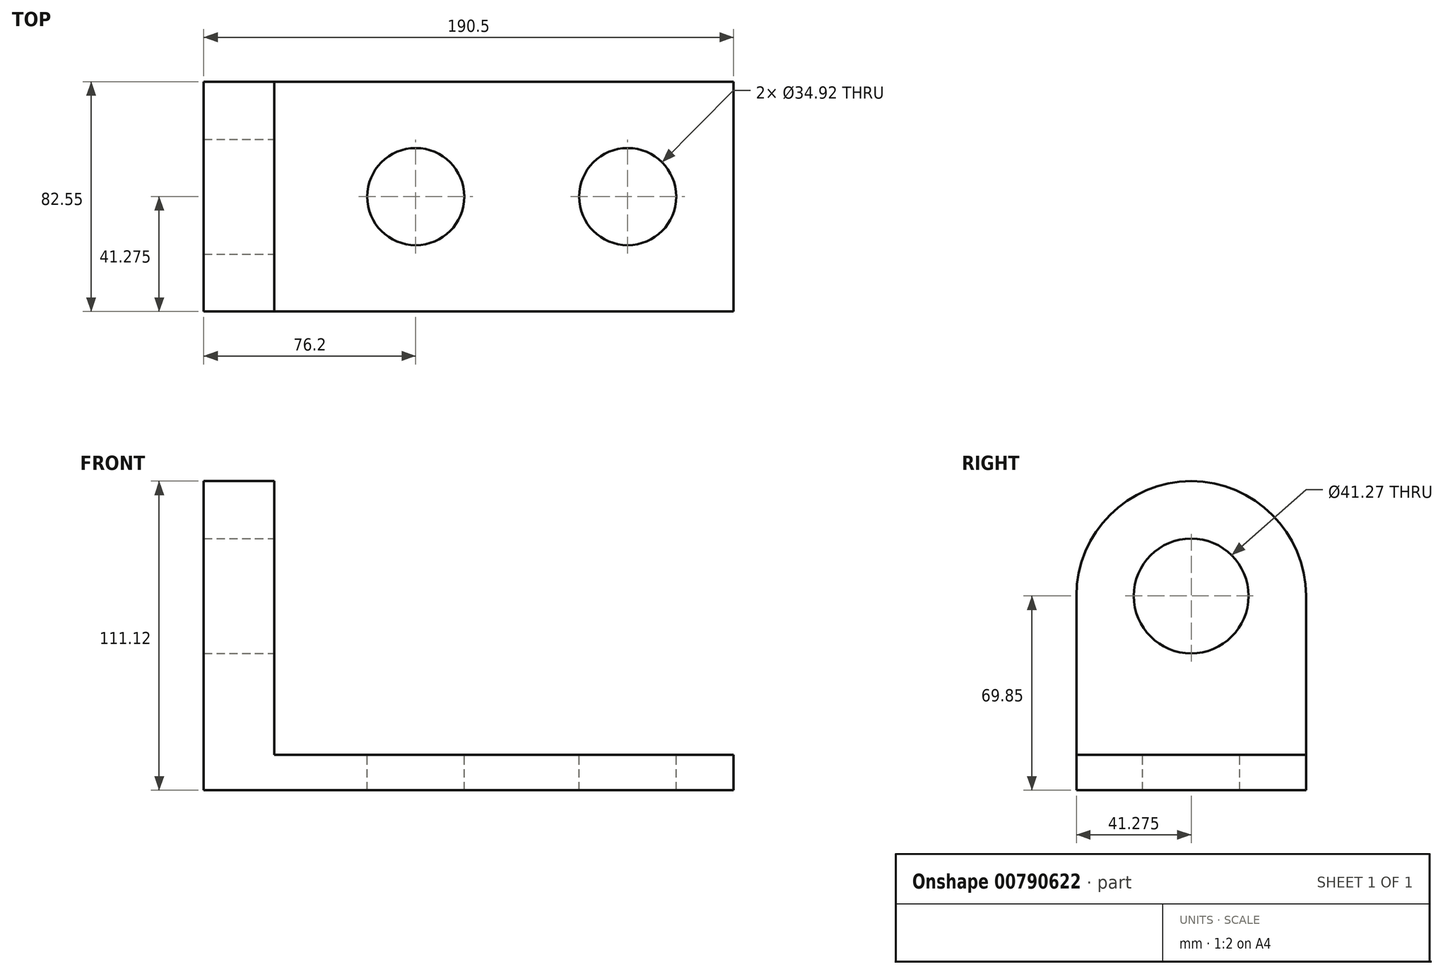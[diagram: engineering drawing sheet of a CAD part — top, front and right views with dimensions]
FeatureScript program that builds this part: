
annotation { "Feature Type Name" : "Feature", "Feature Type Description" : "" }
export const myFeature = defineFeature(function(context is Context, id is Id, definition is map)
    precondition{}
    {
        {
            var Q0;
            Q0=qCreatedBy(makeId("Front.planeOp"),FACE);
            var sketch = newSketch(context, id + "F0", { "sketchPlane" : qUnion([Q0])});
            skLineSegment(sketch, "E0", {"start": v(0, 0) * mm, "end": v(-95.25, 0) * mm});
            skLineSegment(sketch, "E1", {"start": v(0, 0) * mm, "end": v(95.25, 0) * mm});
            skLineSegment(sketch, "E2", {"start": v(-95.25, 0) * mm, "end": v(-95.25, 57.15) * mm});
            skLineSegment(sketch, "E3", {"start": v(-95.25, 57.15) * mm, "end": v(-69.85, 57.15) * mm});
            skLineSegment(sketch, "E4", {"start": v(95.25, 0) * mm, "end": v(95.25, 12.7) * mm});
            skLineSegment(sketch, "E5", {"start": v(95.25, 12.7) * mm, "end": v(-69.85, 12.7) * mm});
            skLineSegment(sketch, "E6", {"start": v(-69.85, 57.15) * mm, "end": v(-69.85, 12.7) * mm});
            skSolve(sketch);
        }
        {
            var Q0;
            Q0 = qSketchRegion(id + "F0", true);
            extrude(context, id + "F1", {"entities" : qUnion([Q0]), "depth" : 82.55 * mm, "offsetDistance" : 25.4 * mm});
        }
        {
            var Q0;
            Q0=makeQuery(id+"F1.opExtrude","SWEPT_FACE",FACE,{"disambiguationData":[OSD([sQuery(id+"F0.wireOp",EDGE,"E5")])]});
            var sketch = newSketch(context, id + "F2", { "sketchPlane" : qUnion([Q0])});
            skLineSegment(sketch, "E7", {"start": v(95.25, -41.28) * mm, "end": v(57.15, -41.28) * mm, "construction": true});
            skLineSegment(sketch, "E8", {"start": v(57.15, -41.28) * mm, "end": v(-19.05, -41.28) * mm, "construction": true});
            skCircle(sketch, "E9", {"center": v(-19.05, -41.28) * mm, "radius": 17.46 * mm, "construction": true});
            skCircle(sketch, "E10", {"center": v(57.15, -41.28) * mm, "radius": 17.46 * mm, "construction": true});
            skCircle(sketch, "E11", {"center": v(-19.05, -41.28) * mm, "radius": 17.46 * mm});
            skCircle(sketch, "E12", {"center": v(57.15, -41.28) * mm, "radius": 17.46 * mm});
            skSolve(sketch);
        }
        {
            var Q0;
            Q0=makeQuery(id+"F2.imprint","IMPRINT",FACE,{"disambiguationData":[TD([[makeQuery(id+"F2.imprint","IMPRINT",EDGE,{"derivedFrom":sQuery(id+"F2.wireOp",EDGE,"E11")}),1.0]])]});
            extrude(context, id + "F3", {"entities" : qUnion([Q0]), "operationType" : NewBodyOperationType.REMOVE, "oppositeDirection" : true, "depth" : 12.7 * mm, "offsetDistance" : 25.4 * mm});
        }
        {
            var Q0;
            Q0=makeQuery(id+"F1.opExtrude","SWEPT_FACE",FACE,{"disambiguationData":[OSD([sQuery(id+"F0.wireOp",EDGE,"E5")])]});
            var sketch = newSketch(context, id + "F4", { "sketchPlane" : qUnion([Q0])});
            skLineSegment(sketch, "E13", {"start": v(95.25, -41.28) * mm, "end": v(57.15, -41.28) * mm, "construction": true});
            skCircle(sketch, "E14", {"center": v(57.15, -41.28) * mm, "radius": 17.46 * mm});
            skSolve(sketch);
        }
        {
            var Q0;
            Q0=makeQuery(id+"F4.imprint","IMPRINT",FACE,{"disambiguationData":[TD([[makeQuery(id+"F4.imprint","IMPRINT",EDGE,{"derivedFrom":sQuery(id+"F4.wireOp",EDGE,"E14")}),1.0]])]});
            extrude(context, id + "F5", {"entities" : qUnion([Q0]), "operationType" : NewBodyOperationType.REMOVE, "oppositeDirection" : true, "depth" : 12.7 * mm, "offsetDistance" : 25.4 * mm});
        }
        {
            var Q0;
            Q0=makeQuery(id+"F1.opExtrude","SWEPT_FACE",FACE,{"disambiguationData":[OSD([sQuery(id+"F0.wireOp",EDGE,"E3")])]});
            extrude(context, id + "F6", {"entities" : qUnion([Q0]), "operationType" : NewBodyOperationType.ADD, "depth" : 57.15 * mm, "offsetDistance" : 25.4 * mm});
        }
        {
            var Q0;
            {var subQ0=sQuery(id+"F0.wireOp",EDGE,"E6");Q0=makeQuery(id+"F6.boolean.opBoolean","MERGE",FACE,{"derivedFrom":[makeQuery(id+"F1.opExtrude","SWEPT_FACE",FACE,{"disambiguationData":[OSD([subQ0])]}),makeQuery(id+"F6.opExtrude","SWEPT_FACE",FACE,{"disambiguationData":[OSD([sQuery(id+"F0.wireOp",EDGE,"E3"),subQ0])]})]});}
            var sketch = newSketch(context, id + "F7", { "sketchPlane" : qUnion([Q0])});
            skLineSegment(sketch, "E15", {"start": v(-82.55, 12.7) * mm, "end": v(-82.55, 69.85) * mm, "construction": true});
            skLineSegment(sketch, "E16", {"start": v(0, 12.7) * mm, "end": v(0, 69.85) * mm, "construction": true});
            skArc(sketch, "E17", {"start": v(0, 69.85) * mm, "mid": v(-41.28, 111.13) * mm, "end": v(-82.55, 69.85) * mm});
            skSolve(sketch);
        }
        {
            var Q0;
            {var subQ0=sQuery(id+"F7.wireOp",EDGE,"E17");Q0=makeQuery(id+"F7.imprint","IMPRINT",FACE,{"disambiguationData":[TD([[makeQuery(id+"F7.imprint","IMPRINT",EDGE,{"derivedFrom":subQ0}),-1.0]])]});}
            extrude(context, id + "F8", {"entities" : qUnion([Q0]), "operationType" : NewBodyOperationType.REMOVE, "oppositeDirection" : true, "depth" : 25.4 * mm, "offsetDistance" : 25.4 * mm});
        }
        {
            var Q0;
            {var subQ0=sQuery(id+"F0.wireOp",EDGE,"E6");Q0=makeQuery(id+"F6.boolean.opBoolean","MERGE",FACE,{"derivedFrom":[makeQuery(id+"F1.opExtrude","SWEPT_FACE",FACE,{"disambiguationData":[OSD([subQ0])]}),makeQuery(id+"F6.opExtrude","SWEPT_FACE",FACE,{"disambiguationData":[OSD([sQuery(id+"F0.wireOp",EDGE,"E3"),subQ0])]})]});}
            var sketch = newSketch(context, id + "F9", { "sketchPlane" : qUnion([Q0])});
            skLineSegment(sketch, "E18", {"start": v(-82.55, 69.85) * mm, "end": v(-41.28, 69.85) * mm, "construction": true});
            skCircle(sketch, "E19", {"center": v(-41.28, 69.85) * mm, "radius": 20.64 * mm});
            skSolve(sketch);
        }
        {
            var Q0;
            Q0=makeQuery(id+"F9.imprint","IMPRINT",FACE,{"disambiguationData":[TD([[makeQuery(id+"F9.imprint","IMPRINT",EDGE,{"derivedFrom":sQuery(id+"F9.wireOp",EDGE,"E19")}),1.0]])]});
            extrude(context, id + "F10", {"entities" : qUnion([Q0]), "operationType" : NewBodyOperationType.REMOVE, "oppositeDirection" : true, "depth" : 25.4 * mm, "offsetDistance" : 25.4 * mm});
        }
    });
